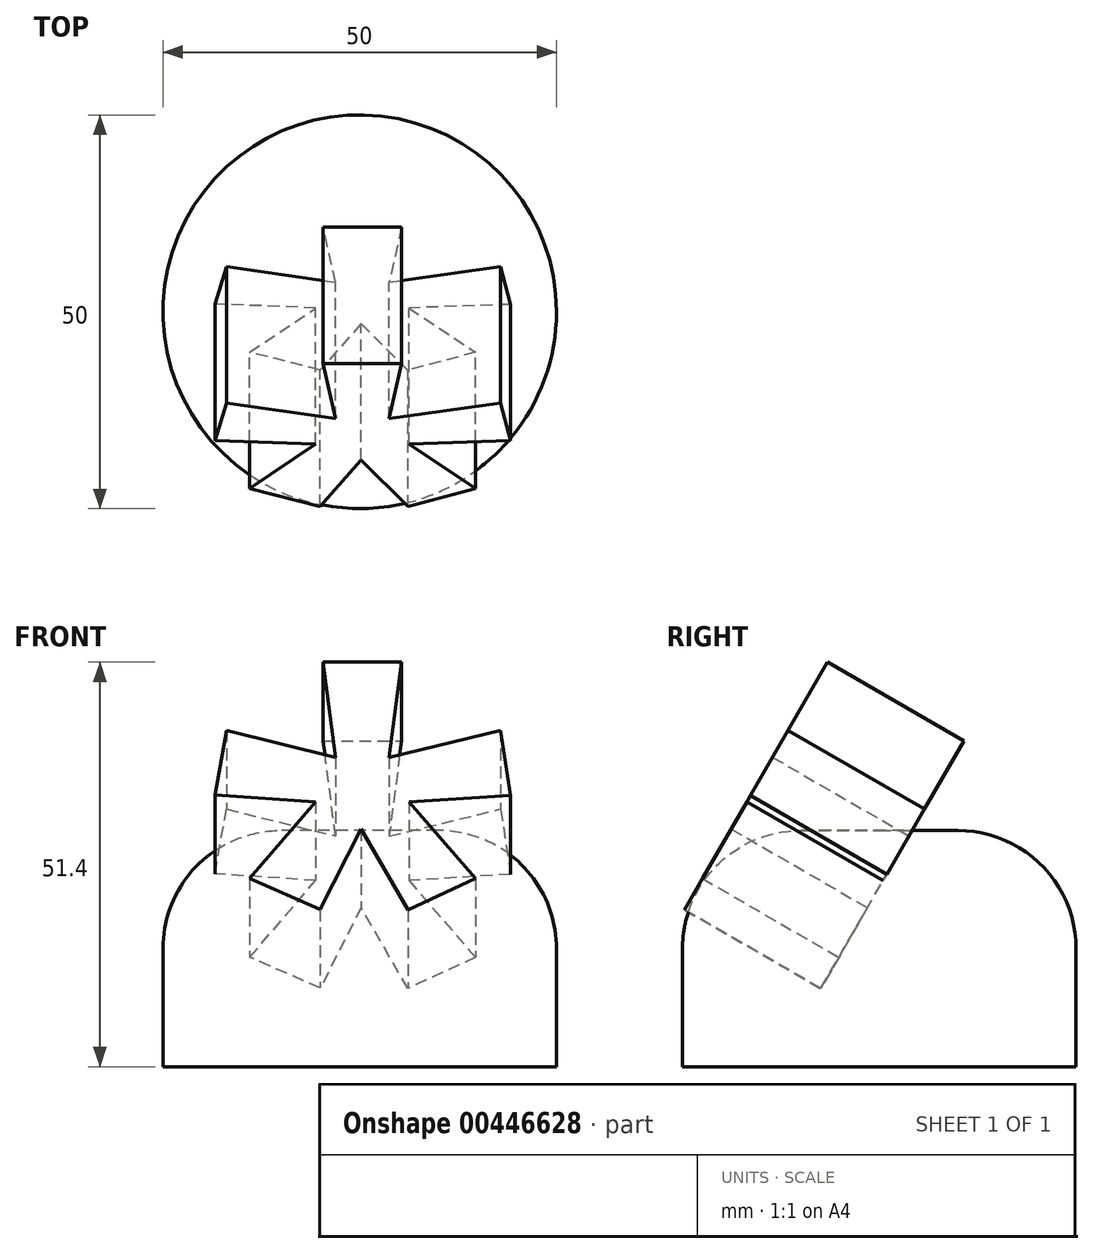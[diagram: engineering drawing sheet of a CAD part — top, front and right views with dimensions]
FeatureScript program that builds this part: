
annotation { "Feature Type Name" : "Feature", "Feature Type Description" : "" }
export const myFeature = defineFeature(function(context is Context, id is Id, definition is map)
    precondition{}
    {
        {
            var Q0;
            Q0=qCreatedBy(makeId("Top.planeOp"),FACE);
            var sketch = newSketch(context, id + "F0", { "sketchPlane" : qUnion([Q0])});
            skText(sketch, "E0", { "text": "*", "fontName": "OpenSans-Bold.ttf"});
            const initialGuessF0  = {"E0": [-0.09905, -0.03772, 1, 0, 0.05595]};
            skSetInitialGuess(sketch, initialGuessF0);
            skSolve(sketch);
        }
        {
            var Q0;
            Q0=qSketchRegion(id+"F0",true);
            extrude(context, id + "F1", {"entities" : qUnion([Q0]), "depth" : 20 * mm});
        }
        {
            var Q0;
            Q0=makeQuery(id+"F1.opExtrude","SWEPT_BODY",BODY,{"disambiguationData":[OSD([sQuery(id+"F0.wireOp",EDGE,"E0.sketch_text.stroke-0"),sQuery(id+"F0.wireOp",EDGE,"E0.sketch_text.stroke-1"),sQuery(id+"F0.wireOp",EDGE,"E0.sketch_text.stroke-2"),sQuery(id+"F0.wireOp",EDGE,"E0.sketch_text.stroke-3"),sQuery(id+"F0.wireOp",EDGE,"E0.sketch_text.stroke-4"),sQuery(id+"F0.wireOp",EDGE,"E0.sketch_text.stroke-5"),sQuery(id+"F0.wireOp",EDGE,"E0.sketch_text.stroke-6"),sQuery(id+"F0.wireOp",EDGE,"E0.sketch_text.stroke-7"),sQuery(id+"F0.wireOp",EDGE,"E0.sketch_text.stroke-8"),sQuery(id+"F0.wireOp",EDGE,"E0.sketch_text.stroke-9"),sQuery(id+"F0.wireOp",EDGE,"E0.sketch_text.stroke-10"),sQuery(id+"F0.wireOp",EDGE,"E0.sketch_text.stroke-11"),sQuery(id+"F0.wireOp",EDGE,"E0.sketch_text.stroke-12"),sQuery(id+"F0.wireOp",EDGE,"E0.sketch_text.stroke-13")])]});
            transform(context, id + "F2", {"entities" : qUnion([Q0]), "transformType" : TransformType.TRANSLATION_3D, "dx" : 76.45 * mm, "dy" : 0 * mm, "dz" : 0 * mm, "makeCopy" : false});
        }
        {
            var Q0;
            Q0=qCreatedBy(makeId("Top.planeOp"),FACE);
            var sketch = newSketch(context, id + "F3", { "sketchPlane" : qUnion([Q0])});
            skCircle(sketch, "E1", {"center": v(-27.2, 27.91) * mm, "radius": 25 * mm});
            skSolve(sketch);
        }
        {
            var Q0;
            Q0=makeQuery(id+"F1.opExtrude","SWEPT_BODY",BODY,{"disambiguationData":[OSD([sQuery(id+"F0.wireOp",EDGE,"E0.sketch_text.stroke-0"),sQuery(id+"F0.wireOp",EDGE,"E0.sketch_text.stroke-1"),sQuery(id+"F0.wireOp",EDGE,"E0.sketch_text.stroke-2"),sQuery(id+"F0.wireOp",EDGE,"E0.sketch_text.stroke-3"),sQuery(id+"F0.wireOp",EDGE,"E0.sketch_text.stroke-4"),sQuery(id+"F0.wireOp",EDGE,"E0.sketch_text.stroke-5"),sQuery(id+"F0.wireOp",EDGE,"E0.sketch_text.stroke-6"),sQuery(id+"F0.wireOp",EDGE,"E0.sketch_text.stroke-7"),sQuery(id+"F0.wireOp",EDGE,"E0.sketch_text.stroke-8"),sQuery(id+"F0.wireOp",EDGE,"E0.sketch_text.stroke-9"),sQuery(id+"F0.wireOp",EDGE,"E0.sketch_text.stroke-10"),sQuery(id+"F0.wireOp",EDGE,"E0.sketch_text.stroke-11"),sQuery(id+"F0.wireOp",EDGE,"E0.sketch_text.stroke-12"),sQuery(id+"F0.wireOp",EDGE,"E0.sketch_text.stroke-13")])]});
            transform(context, id + "F4", {"entities" : qUnion([Q0]), "transformType" : TransformType.TRANSLATION_3D, "dx" : 27.3 * mm, "dy" : 0 * mm, "dz" : 0 * mm, "makeCopy" : false});
        }
        {
            var Q0;
            Q0=makeQuery(id+"F3.imprint","IMPRINT",FACE,{"disambiguationData":[TD([[makeQuery(id+"F3.imprint","IMPRINT",EDGE,{"derivedFrom":sQuery(id+"F3.wireOp",EDGE,"E1")}),1.0]])]});
            extrude(context, id + "F5", {"entities" : qUnion([Q0]), "depth" : 30 * mm});
        }
        {
            var Q0;
            Q0=makeQuery(id+"F5.opExtrude","CAP_FACE",FACE,{"disambiguationData":[OSD([sQuery(id+"F3.wireOp",EDGE,"E1")])],"isStart":false});
            fillet(context, id + "F6", {"entities" : qUnion([Q0]), "radius" : 15 * mm, "tangentPropagation" : true, "allowEdgeOverflow" : false});
        }
        {
            var Q0;
            Q0=makeQuery(id+"F1.opExtrude","SWEPT_BODY",BODY,{"disambiguationData":[OSD([sQuery(id+"F0.wireOp",EDGE,"E0.sketch_text.stroke-0"),sQuery(id+"F0.wireOp",EDGE,"E0.sketch_text.stroke-1"),sQuery(id+"F0.wireOp",EDGE,"E0.sketch_text.stroke-2"),sQuery(id+"F0.wireOp",EDGE,"E0.sketch_text.stroke-3"),sQuery(id+"F0.wireOp",EDGE,"E0.sketch_text.stroke-4"),sQuery(id+"F0.wireOp",EDGE,"E0.sketch_text.stroke-5"),sQuery(id+"F0.wireOp",EDGE,"E0.sketch_text.stroke-6"),sQuery(id+"F0.wireOp",EDGE,"E0.sketch_text.stroke-7"),sQuery(id+"F0.wireOp",EDGE,"E0.sketch_text.stroke-8"),sQuery(id+"F0.wireOp",EDGE,"E0.sketch_text.stroke-9"),sQuery(id+"F0.wireOp",EDGE,"E0.sketch_text.stroke-10"),sQuery(id+"F0.wireOp",EDGE,"E0.sketch_text.stroke-11"),sQuery(id+"F0.wireOp",EDGE,"E0.sketch_text.stroke-12"),sQuery(id+"F0.wireOp",EDGE,"E0.sketch_text.stroke-13")])]});
            var Q1;
            Q1=makeQuery(id+"F1.opExtrude","CAP_EDGE",EDGE,{"disambiguationData":[OSD([sQuery(id+"F0.wireOp",EDGE,"E0.sketch_text.stroke-14")])],"isStart":false});
            transform(context, id + "F7", {"entities" : qUnion([Q0]), "transformType" : TransformType.ROTATION, "transformAxis" : qUnion([Q1]), "angle" : 60 * degree, "makeCopy" : false});
        }
        {
            var Q0;
            Q0=makeQuery(id+"F1.opExtrude","SWEPT_BODY",BODY,{"disambiguationData":[OSD([sQuery(id+"F0.wireOp",EDGE,"E0.sketch_text.stroke-0"),sQuery(id+"F0.wireOp",EDGE,"E0.sketch_text.stroke-1"),sQuery(id+"F0.wireOp",EDGE,"E0.sketch_text.stroke-2"),sQuery(id+"F0.wireOp",EDGE,"E0.sketch_text.stroke-3"),sQuery(id+"F0.wireOp",EDGE,"E0.sketch_text.stroke-4"),sQuery(id+"F0.wireOp",EDGE,"E0.sketch_text.stroke-5"),sQuery(id+"F0.wireOp",EDGE,"E0.sketch_text.stroke-6"),sQuery(id+"F0.wireOp",EDGE,"E0.sketch_text.stroke-7"),sQuery(id+"F0.wireOp",EDGE,"E0.sketch_text.stroke-8"),sQuery(id+"F0.wireOp",EDGE,"E0.sketch_text.stroke-9"),sQuery(id+"F0.wireOp",EDGE,"E0.sketch_text.stroke-10"),sQuery(id+"F0.wireOp",EDGE,"E0.sketch_text.stroke-11"),sQuery(id+"F0.wireOp",EDGE,"E0.sketch_text.stroke-12"),sQuery(id+"F0.wireOp",EDGE,"E0.sketch_text.stroke-13")])]});
            transform(context, id + "F8", {"entities" : qUnion([Q0]), "transformType" : TransformType.TRANSLATION_3D, "dx" : -52.7 * mm, "dy" : 0 * mm, "dz" : 31.4 * mm, "makeCopy" : false});
        }
    });
